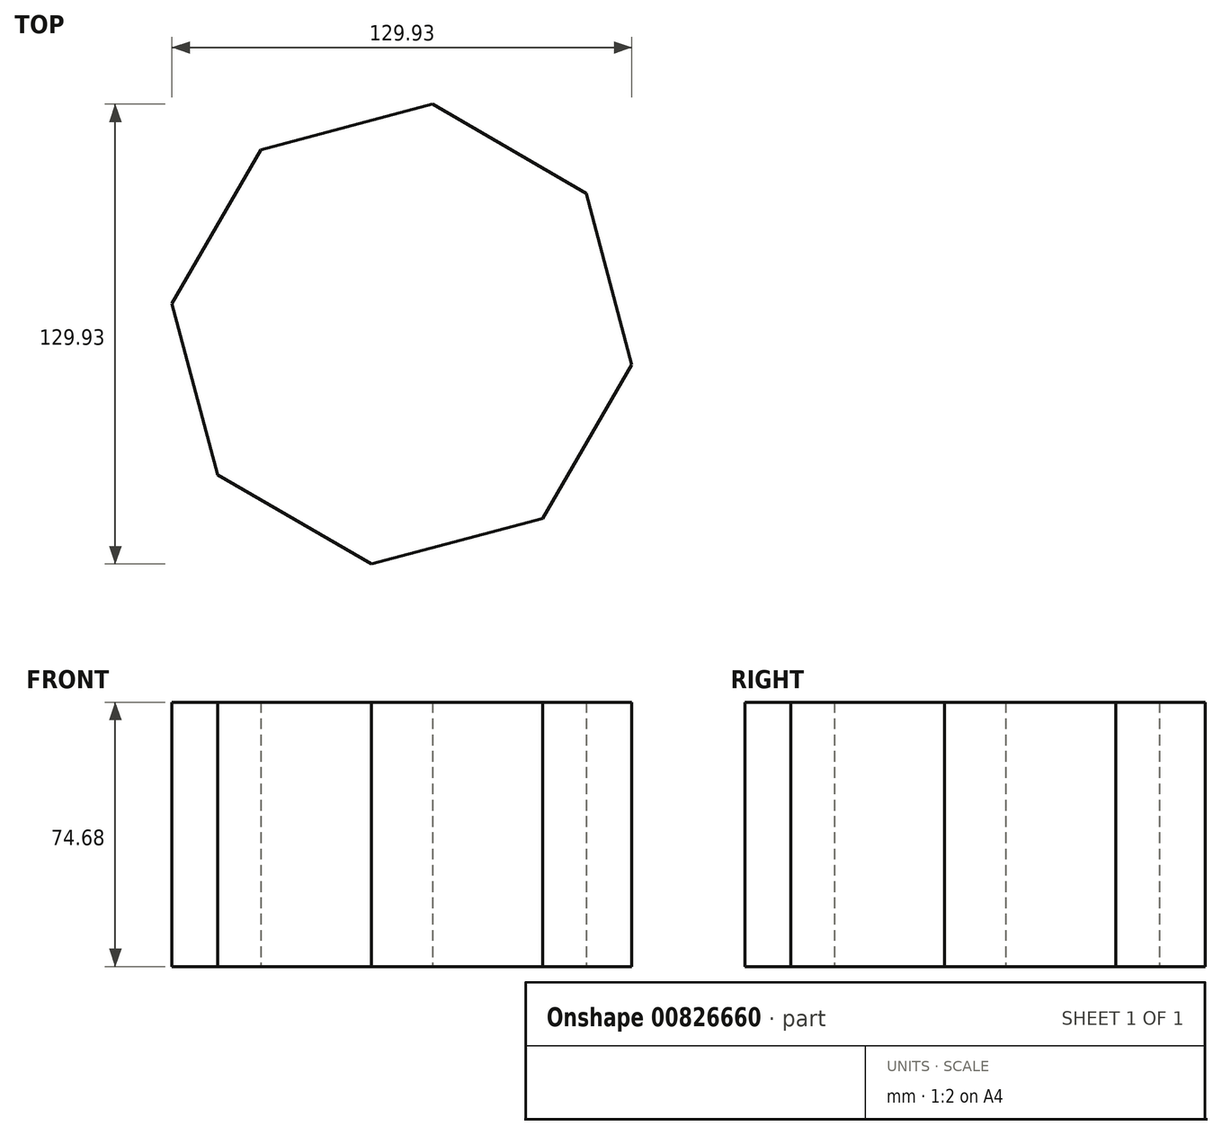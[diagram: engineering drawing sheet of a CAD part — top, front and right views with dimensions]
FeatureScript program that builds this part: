
annotation { "Feature Type Name" : "Feature", "Feature Type Description" : "" }
export const myFeature = defineFeature(function(context is Context, id is Id, definition is map)
    precondition{}
    {
        {
            var Q0;
            Q0=qCreatedBy(makeId("Top.planeOp"),FACE);
            var sketch = newSketch(context, id + "F0", { "sketchPlane" : qUnion([Q0])});
            skCircle(sketch, "E0.cCircle", {"center": v(-40.05, 42.9) * mm, "radius": 60.55 * mm, "construction": true});
            skLineSegment(sketch, "E0.0", {"start": v(-48.72, -22.07) * mm, "end": v(-92.11, 3.09) * mm});
            skLineSegment(sketch, "E0.1", {"start": v(-92.11, 3.09) * mm, "end": v(-105.01, 51.56) * mm});
            skLineSegment(sketch, "E0.2", {"start": v(-105.01, 51.56) * mm, "end": v(-79.85, 94.96) * mm});
            skLineSegment(sketch, "E0.3", {"start": v(-79.85, 94.96) * mm, "end": v(-31.38, 107.86) * mm});
            skLineSegment(sketch, "E0.4", {"start": v(-31.38, 107.86) * mm, "end": v(12.02, 82.7) * mm});
            skLineSegment(sketch, "E0.5", {"start": v(12.02, 82.7) * mm, "end": v(24.92, 34.23) * mm});
            skLineSegment(sketch, "E0.6", {"start": v(24.92, 34.23) * mm, "end": v(-0.24, -9.17) * mm});
            skLineSegment(sketch, "E0.7", {"start": v(-0.24, -9.17) * mm, "end": v(-48.72, -22.07) * mm});
            skPoint(sketch, "E0.0.midPoint", {"position": v(-70.42, -9.49) * mm});
            skSolve(sketch);
        }
        {
            var Q0;
            Q0=makeQuery(id+"F0.imprint","IMPRINT",FACE,{"disambiguationData":[TD([[makeQuery(id+"F0.imprint","IMPRINT",EDGE,{"derivedFrom":sQuery(id+"F0.wireOp",EDGE,"E0.0")}),-1.0]])]});
            extrude(context, id + "F1", {"entities" : qUnion([Q0]), "endBound" : BoundingType.SYMMETRIC, "depth" : 74.68 * mm, "offsetDistance" : 25.4 * mm});
        }
    });
